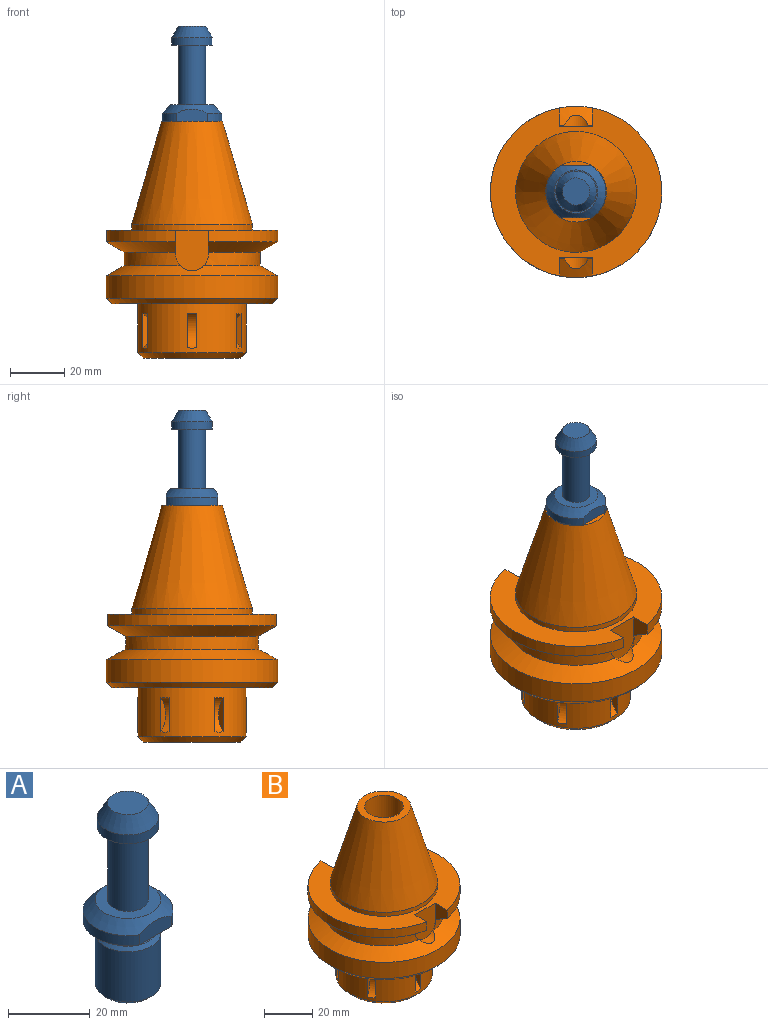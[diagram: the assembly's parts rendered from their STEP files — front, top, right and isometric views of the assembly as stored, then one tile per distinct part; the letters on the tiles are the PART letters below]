
ASSEMBLY  parts=2 mates=1
PART A: 18 faces, bbox 22x22x55 mm
  f0: plane 22x19mm, normal (0,0,-1), area 279.1mm2, adj f1,f2,f9,f16,f17
  f1: cylinder r=11mm len=19mm, axis (0,0,-1), area 68.8mm2, adj f0,f3,f16,f17
  f2: cylinder r=11mm len=19mm, axis (0,0,-1), area 68.8mm2, adj f0,f3,f16,f17
  f3: cone r=8mm half-angle=45deg, axis (0,0,-1), area 221.4mm2, adj f1,f2,f10,f16,f17
  f4: plane 14x14mm, normal (0,0,-1), area 153.9mm2, adj f5
  f5: cone r=7mm half-angle=45deg, axis (0,0,1), area 66.6mm2, adj f4,f6
  f6: cylinder r=8mm len=16mm, axis (0,0,-1), area 754mm2, adj f5,f7
  f7: cone r=8mm half-angle=45deg, axis (0,0,-1), area 66.6mm2, adj f6,f8
  f8: plane 14x14mm, normal (0,0,1), area 75.4mm2, adj f7,f9
  f9: cylinder r=5mm len=10mm, axis (0,0,-1), area 94.2mm2, adj f0,f8
  f10: plane 16x16mm, normal (0,0,1), area 122.5mm2, adj f3,f11
  f11: cylinder r=5mm len=22mm, axis (0,0,-1), area 691.2mm2, adj f10,f12
  f12: plane 15x15mm, normal (0,0,-1), area 98.2mm2, adj f11,f13
  f13: cylinder r=7.5mm len=15mm, axis (0,0,-1), area 125.8mm2, adj f12,f14
  f14: cone r=7.5mm half-angle=30deg, axis (0,0,-1), area 196.3mm2, adj f13,f15
  f15: plane 10x10mm, normal (0,0,1), area 78.5mm2, adj f14
  f16: plane 11.11x4.5mm, normal (0,1,0), area 44.2mm2, adj f0,f1,f2,f3
  f17: plane 11.11x4.5mm, normal (0,-1,0), area 44.2mm2, adj f0,f1,f2,f3
PART B: 44 faces, bbox 63.2x63.2x87.2 mm
  f0: cylinder r=20mm len=40mm, axis (0,0,-1), area 1997.2mm2, adj f10,f11,f26,f27,f28,f29,f30,f31
  f1: cylinder r=31.5mm len=61.85mm, axis (0,0,-1), area 378mm2, adj f6,f15,f18,f22
  f2: cylinder r=31.5mm len=61.85mm, axis (0,0,-1), area 378mm2, adj f14,f15,f20,f23
  f3: cone r=25mm half-angle=60deg, axis (0,0,-1), area 1286.9mm2, adj f4,f5,f13,f19,f24
  f4: cylinder r=25mm len=49.23mm, axis (0,0,-1), area 336.1mm2, adj f3,f6,f18,f19,f22,f24
  f5: cylinder r=25mm len=49.23mm, axis (0,0,-1), area 336.1mm2, adj f3,f14,f19,f20,f23,f24
  f6: cone r=31.5mm half-angle=60deg, axis (0,0,1), area 574.5mm2, adj f1,f4,f18,f22
  f7: plane 22.3x22.3mm, normal (0,0,1), area 189.4mm2, adj f8,f17
  f8: cylinder r=8mm len=87mm, axis (0,0,-1), area 4373.1mm2, adj f7,f9
  f9: plane 36x36mm, normal (0,0,-1), area 816.8mm2, adj f8,f10
  f10: cone r=18mm half-angle=45deg, axis (0,0,1), area 337.7mm2, adj f0,f9
  f11: plane 59x59mm, normal (0,0,-1), area 1477.3mm2, adj f0,f12
  f12: cone r=29.5mm half-angle=45deg, axis (0,0,1), area 542mm2, adj f11,f13
  f13: cylinder r=31.5mm len=63mm, axis (0,0,-1), area 1613.1mm2, adj f3,f12
  f14: cone r=31.5mm half-angle=60deg, axis (0,0,1), area 574.5mm2, adj f2,f5,f20,f23
  f15: plane 63x61.85mm, normal (0,0,1), area 1390.1mm2, adj f1,f2,f16,f18,f20,f21,f22,f23
  f16: cylinder r=22.23mm len=44.45mm, axis (0,0,-1), area 279.3mm2, adj f15,f17
  f17: cone r=22.23mm half-angle=16.2deg, axis (0,0,-1), area 4150mm2, adj f7,f16
  f18: plane 9.14x7.09mm, normal (1,0,0), area 43.9mm2, adj f1,f4,f6,f15,f19,f21
  f19: cylinder r=6mm len=12mm, axis (0,-1,0), area 33.4mm2, adj f3,f4,f5,f18,f20,f21
  f20: plane 9.14x7.09mm, normal (-1,0,0), area 43.9mm2, adj f2,f5,f14,f15,f19,f21
  f21: plane 14.97x12mm, normal (0,-1,0), area 164.2mm2, adj f15,f18,f19,f20
  f22: plane 9.14x7.09mm, normal (1,0,0), area 43.9mm2, adj f1,f4,f6,f15,f24,f25
  f23: plane 9.14x7.09mm, normal (-1,0,0), area 43.9mm2, adj f2,f5,f14,f15,f24,f25
  f24: cylinder r=6mm len=12mm, axis (0,1,0), area 33.4mm2, adj f3,f4,f5,f22,f23,f25
  f25: plane 14.97x12mm, normal (0,1,0), area 164.2mm2, adj f15,f22,f23,f24
  f26: cylinder r=7.5mm len=12.59mm, axis (-1,0,0), area 52.3mm2, adj f0,f27,f28
  f27: plane 12.59x3.42mm, normal (-1,0,0), area 30.4mm2, adj f0,f26
  f28: plane 12.59x3.42mm, normal (1,0,0), area 30.4mm2, adj f0,f26
  f29: cylinder r=7.5mm len=12.59mm, axis (-1,0,0), area 52.3mm2, adj f0,f30,f31
  f30: plane 12.59x3.42mm, normal (-1,0,0), area 30.4mm2, adj f0,f29
  f31: plane 12.59x3.42mm, normal (1,0,0), area 30.4mm2, adj f0,f29
  f32: cylinder r=7.5mm len=12.59mm, axis (0.5,-0.87,0), area 52.3mm2, adj f0,f33,f34
  f33: plane 12.59x2.96mm, normal (0.5,-0.87,0), area 30.4mm2, adj f0,f32
  f34: plane 12.59x2.96mm, normal (-0.5,0.87,0), area 30.4mm2, adj f0,f32
  f35: cylinder r=7.5mm len=12.59mm, axis (0.5,-0.87,0), area 52.3mm2, adj f0,f36,f37
  f36: plane 12.59x2.96mm, normal (0.5,-0.87,0), area 30.4mm2, adj f0,f35
  f37: plane 12.59x2.96mm, normal (-0.5,0.87,0), area 30.4mm2, adj f0,f35
  f38: cylinder r=7.5mm len=12.59mm, axis (0.5,0.87,0), area 52.3mm2, adj f0,f39,f40
  f39: plane 12.59x2.96mm, normal (0.5,0.87,0), area 30.4mm2, adj f0,f38
  f40: plane 12.59x2.96mm, normal (-0.5,-0.87,0), area 30.4mm2, adj f0,f38
  f41: cylinder r=7.5mm len=12.59mm, axis (0.5,0.87,0), area 52.3mm2, adj f0,f42,f43
  f42: plane 12.59x2.96mm, normal (0.5,0.87,0), area 30.4mm2, adj f0,f41
  f43: plane 12.59x2.96mm, normal (-0.5,-0.87,0), area 30.4mm2, adj f0,f41
PLACE A t=(-22.54,-12.27,-58.9)mm
PLACE B t=(-22.54,-12.27,4.62)mm fixed
MATE fastened B.f0 <-> A.f1  axis (0,0,1) through (-22.54,-12.27,44.62)mm
